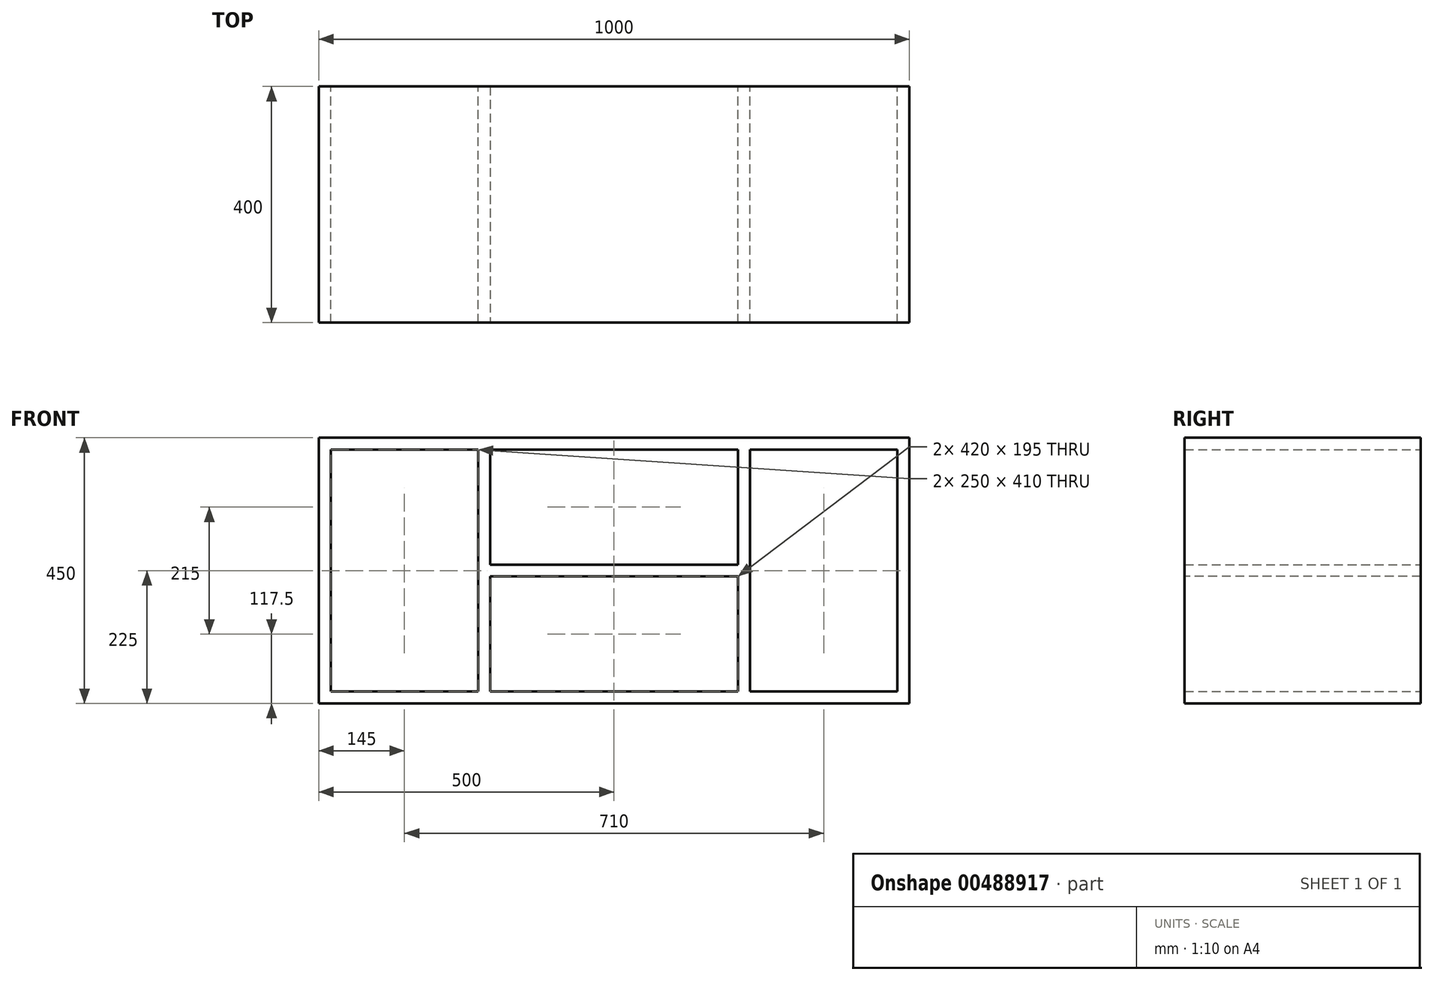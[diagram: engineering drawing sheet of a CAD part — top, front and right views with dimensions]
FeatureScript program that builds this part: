
annotation { "Feature Type Name" : "Feature", "Feature Type Description" : "" }
export const myFeature = defineFeature(function(context is Context, id is Id, definition is map)
    precondition{}
    {
        {
            var Q0;
            Q0=qCreatedBy(makeId("Front.planeOp"),FACE);
            var sketch = newSketch(context, id + "F0", { "sketchPlane" : qUnion([Q0])});
            skLineSegment(sketch, "E0.bottom", {"start": v(500, -225) * mm, "end": v(-500, -225) * mm});
            skLineSegment(sketch, "E0.top", {"start": v(500, 225) * mm, "end": v(-500, 225) * mm});
            skLineSegment(sketch, "E0.left", {"start": v(500, -225) * mm, "end": v(500, 225) * mm});
            skLineSegment(sketch, "E0.right", {"start": v(-500, -225) * mm, "end": v(-500, 225) * mm});
            skPoint(sketch, "E0.middle", {"position": v(0, 0) * mm});
            skLineSegment(sketch, "E1.0", {"start": v(480, 205) * mm, "end": v(230, 205) * mm});
            skLineSegment(sketch, "E1.1", {"start": v(480, -205) * mm, "end": v(480, 205) * mm});
            skLineSegment(sketch, "E1.2", {"start": v(480, -205) * mm, "end": v(230, -205) * mm});
            skLineSegment(sketch, "E1.3", {"start": v(-480, -205) * mm, "end": v(-480, 205) * mm});
            skLineSegment(sketch, "E2", {"start": v(-230, 205) * mm, "end": v(-230, -205) * mm});
            skLineSegment(sketch, "E3", {"start": v(-210, 205) * mm, "end": v(-210, -205) * mm});
            skLineSegment(sketch, "E4", {"start": v(230, 205) * mm, "end": v(230, -205) * mm});
            skLineSegment(sketch, "E5", {"start": v(210, 205) * mm, "end": v(210, -205) * mm});
            skLineSegment(sketch, "E6.trimOffspring", {"start": v(-230, 205) * mm, "end": v(-480, 205) * mm});
            skLineSegment(sketch, "E7.trimOffspring", {"start": v(210, 205) * mm, "end": v(-210, 205) * mm});
            skLineSegment(sketch, "E8.trimOffspring", {"start": v(-230, -205) * mm, "end": v(-480, -205) * mm});
            skLineSegment(sketch, "E9.trimOffspring", {"start": v(210, -205) * mm, "end": v(-210, -205) * mm});
            skSolve(sketch);
        }
        {
            var Q0;
            Q0=makeQuery(id+"F0.imprint","IMPRINT",FACE,{"disambiguationData":[TD([[makeQuery(id+"F0.imprint","IMPRINT",EDGE,{"derivedFrom":sQuery(id+"F0.wireOp",EDGE,"E0.bottom")}),-1.0]])]});
            extrude(context, id + "F1", {"entities" : qUnion([Q0]), "depth" : 400 * mm, "symmetric" : true});
        }
        {
            var Q0;
            Q0=makeQuery(id+"F1.opExtrude","SWEPT_FACE",FACE,{"disambiguationData":[OSD([sQuery(id+"F0.wireOp",EDGE,"E5")])]});
            var sketch = newSketch(context, id + "F2", { "sketchPlane" : qUnion([Q0])});
            skLineSegment(sketch, "E10.bottom", {"start": v(200, -10) * mm, "end": v(-200, -10) * mm});
            skLineSegment(sketch, "E10.top", {"start": v(200, 10) * mm, "end": v(-200, 10) * mm});
            skLineSegment(sketch, "E10.left", {"start": v(200, -10) * mm, "end": v(200, 10) * mm});
            skLineSegment(sketch, "E10.right", {"start": v(-200, -10) * mm, "end": v(-200, 10) * mm});
            skPoint(sketch, "E10.middle", {"position": v(0, 0) * mm});
            skPoint(sketch, "E11.middle", {"position": v(87.5, 0) * mm});
            skPoint(sketch, "E12.middle", {"position": v(175, 0) * mm});
            skLineSegment(sketch, "E13", {"start": v(0, 0) * mm, "end": v(0, -205) * mm, "construction": true});
            skSolve(sketch);
        }
        {
            var Q0;
            Q0=makeQuery(id+"F2.imprint","IMPRINT",FACE,{"disambiguationData":[TD([[makeQuery(id+"F2.imprint","IMPRINT",EDGE,{"derivedFrom":sQuery(id+"F2.wireOp",EDGE,"296fe2e8-f908-4387-8241-d6bbdc1cc0684.MirrorCS")}),1.0]])]});
            var Q1;
            Q1=makeQuery(id+"F2.imprint","IMPRINT",FACE,{"disambiguationData":[TD([[makeQuery(id+"F2.imprint","IMPRINT",EDGE,{"derivedFrom":sQuery(id+"F2.wireOp",EDGE,"296fe2e8-f908-4387-8241-d6bbdc1cc0680.MirrorCS")}),1.0]])]});
            var Q2;
            Q2=makeQuery(id+"F2.imprint","IMPRINT",FACE,{"disambiguationData":[TD([[makeQuery(id+"F2.imprint","IMPRINT",EDGE,{"derivedFrom":sQuery(id+"F2.wireOp",EDGE,"E10.bottom")}),-1.0]])]});
            var Q3;
            Q3=makeQuery(id+"F2.imprint","IMPRINT",FACE,{"disambiguationData":[TD([[makeQuery(id+"F2.imprint","IMPRINT",EDGE,{"derivedFrom":sQuery(id+"F2.wireOp",EDGE,"E11.bottom")}),-1.0]])]});
            var Q4;
            Q4=makeQuery(id+"F2.imprint","IMPRINT",FACE,{"disambiguationData":[TD([[makeQuery(id+"F2.imprint","IMPRINT",EDGE,{"derivedFrom":sQuery(id+"F2.wireOp",EDGE,"E12.bottom")}),-1.0]])]});
            var Q5;
            Q5=makeQuery(id+"F1.opExtrude","SWEPT_FACE",FACE,{"disambiguationData":[OSD([sQuery(id+"F0.wireOp",EDGE,"E3")])]});
            extrude(context, id + "F3", {"entities" : qUnion([Q0, Q1, Q2, Q3, Q4]), "operationType" : NewBodyOperationType.ADD, "endBound" : BoundingType.UP_TO_SURFACE, "endBoundEntityFace" : qUnion([Q5]), "depth" : 25 * mm});
        }
    });
